# Revit family: FantiniCosmi_BIM_FF82
name_source: partatom
category: Generic Models
units: mm (PartAtom-declared; Revit-internal decimal feet)

## family parameters
Always vertical = Yes
Can host rebar = No
Cut with Voids When Loaded = No
Part Type = Normal
Room Calculation Point = No
Round Connector Dimension = Use Diameter
Shared = No
Work Plane-Based = No

## types (1)
- Standard
    Ambient temperature = 50°C
    Blade material = stainless steel AISI 301 for pipes from G1” to G8
    Casing material = Antishock thermoplastic
    Catalog web link = https://www.fantinicosmi.it
    Complies with = EN 60947-5-1
    Continuous duty rated current = Ith 10A
    Default Elevation = 0 mm  [stored 0 ft]
    Designer = Carniti
    Electrical connection = Female 6,3 mm
    Ground connection = Yes
    Max pressure = 10 bar
    Part Number = FantiniCosmi_BIM_FF82
    Protection degree = IP65
    Rated insulation voltage = Ui 380V~
    SPDT microswitch, dustproof, compliant with  = UL cUL CSA ENEC
    Sealed cable glande = PG16
    Working temperature = -20 ÷ 110°C

note: [stored X ft] marks values corroborated as IEEE doubles in the binary element streams (Revit-internal decimal feet)

## geometry (parser evidence)
native form markers: Sweep x3
no freeform markers — native parametric forms only
